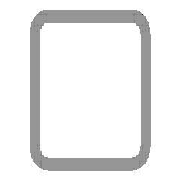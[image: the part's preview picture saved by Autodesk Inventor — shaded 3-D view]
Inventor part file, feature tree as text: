
AUTODESK INVENTOR PART (.ipt)
format: ipt  version: 2025.1 (Build 291241020, 241B)  size: 143,360 bytes
history: native  units: mm (DEFAULTED — no unit token found)
features: other x4, sketch x1, plane x1
ambient origin geometry x8: Origin, YZ Plane, XZ Plane, XY Plane, X Axis, Y Axis, Z Axis, Center Point
bodies: Solid1 (feature_tree), Body (feature_tree)
feature tree (6):
  parser-record x1  (decoder bookkeeping rows leaked as tree rows — omitted from the tree; the rows remain in map.json)
  other  "Driven Length"
  other  "Start Plane"
  other  "End Plane"
  sketch  "Sketch3"  dims[d3=790.0mm d4=0.0mm d7=4.0mm d9=40.0mm d11=40.0mm d12=2.0mm d13=100.0mm d14=890.0mm d15=20.0mm d16=20.0mm d17=90.0deg d18=790.0mm]
  plane  "Work Plane3"
